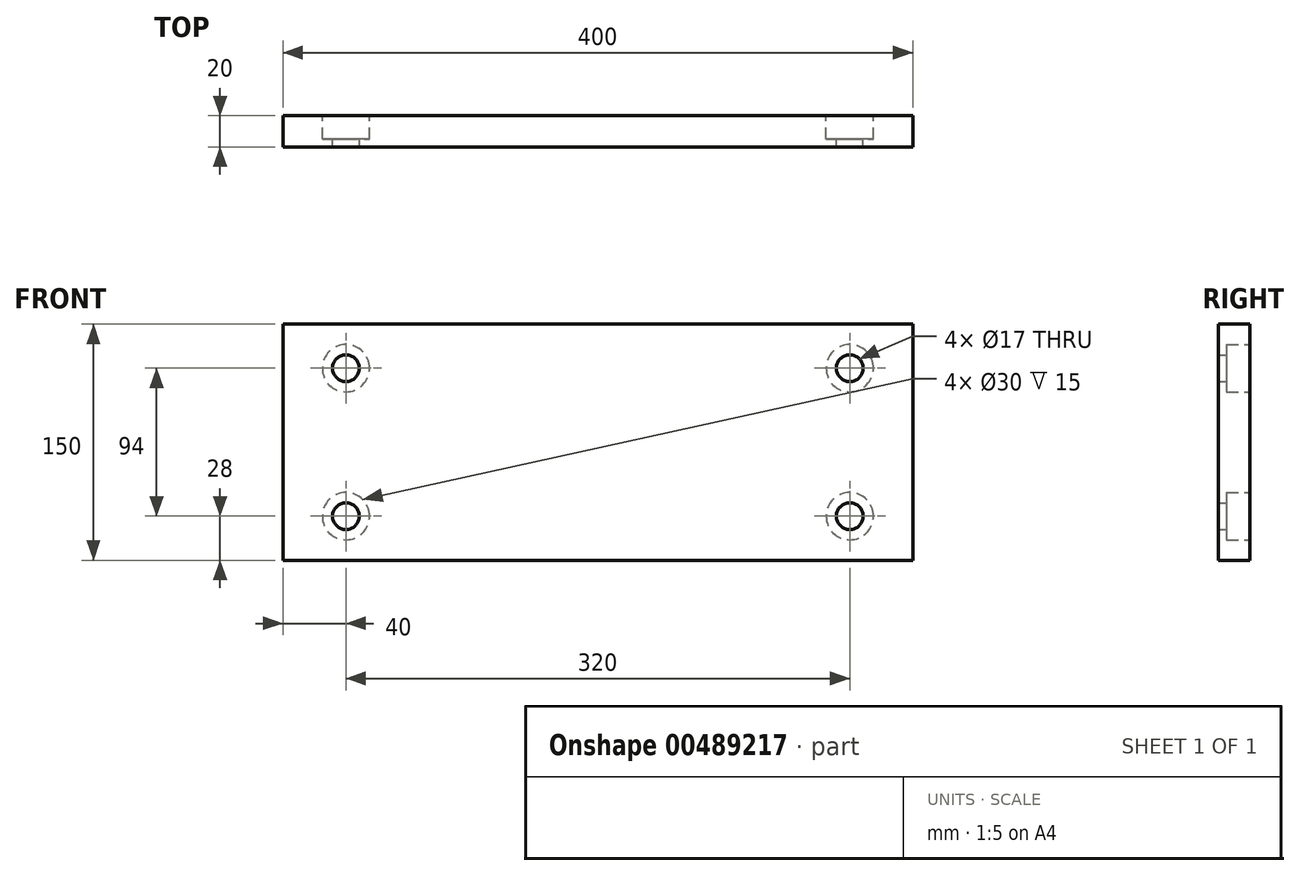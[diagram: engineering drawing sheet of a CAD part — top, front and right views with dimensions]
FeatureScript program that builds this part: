
annotation { "Feature Type Name" : "Feature", "Feature Type Description" : "" }
export const myFeature = defineFeature(function(context is Context, id is Id, definition is map)
    precondition{}
    {
        {
            var Q0;
            Q0=qCreatedBy(makeId("Front.planeOp"),FACE);
            var sketch = newSketch(context, id + "F0", { "sketchPlane" : qUnion([Q0])});
            skLineSegment(sketch, "E0.bottom", {"start": v(0, 0) * mm, "end": v(400, 0) * mm});
            skLineSegment(sketch, "E0.top", {"start": v(0, 150) * mm, "end": v(400, 150) * mm});
            skLineSegment(sketch, "E0.left", {"start": v(0, 0) * mm, "end": v(0, 150) * mm});
            skLineSegment(sketch, "E0.right", {"start": v(400, 0) * mm, "end": v(400, 150) * mm});
            skPoint(sketch, "E1.centerSnap0", {"position": v(400, 75) * mm});
            skPoint(sketch, "E1.centerSnap1", {"position": v(200, 0) * mm});
            skLineSegment(sketch, "E2", {"start": v(200, 75) * mm, "end": v(0, 75) * mm, "construction": true});
            skPoint(sketch, "E3", {"position": v(40, 122) * mm});
            skPoint(sketch, "E4.MirrorP", {"position": v(40, 28) * mm});
            skLineSegment(sketch, "E5", {"start": v(200, 75) * mm, "end": v(200, 182.53) * mm, "construction": true});
            skPoint(sketch, "E5.endSnap0", {"position": v(200, 150) * mm});
            skPoint(sketch, "E6.MirrorP", {"position": v(360, 28) * mm});
            skPoint(sketch, "E7.MirrorP", {"position": v(360, 122) * mm});
            skSolve(sketch);
        }
        {
            var Q0;
            Q0=makeQuery(id+"F0.imprint","IMPRINT",FACE,{"disambiguationData":[TD([[makeQuery(id+"F0.imprint","IMPRINT",EDGE,{"derivedFrom":sQuery(id+"F0.wireOp",EDGE,"E0.bottom")}),1.0]])]});
            extrude(context, id + "F1", {"entities" : qUnion([Q0]), "depth" : 20 * mm, "offsetDistance" : 25 * mm});
        }
        {
            var Q0;
            Q0=sQuery(id+"F0.wireOp",VERTEX,"E7.MirrorP");
            var Q1;
            Q1=sQuery(id+"F0.wireOp",VERTEX,"E6.MirrorP");
            var Q2;
            Q2=sQuery(id+"F0.wireOp",VERTEX,"E3");
            var Q3;
            Q3=sQuery(id+"F0.wireOp",VERTEX,"E4.MirrorP");
            var Q4;
            Q4=makeQuery(id+"F1.opExtrude","SWEPT_BODY",BODY,{"disambiguationData":[OSD([sQuery(id+"F0.wireOp",EDGE,"E0.bottom"),sQuery(id+"F0.wireOp",EDGE,"E0.top"),sQuery(id+"F0.wireOp",EDGE,"E0.left"),sQuery(id+"F0.wireOp",EDGE,"E0.right"),sQuery(id+"F0.wireOp",EDGE,"E1")])]});
            hole(context, id + "F2", {"style" : HoleStyle.C_BORE, "endStyle" : HoleEndStyle.BLIND, "oppositeDirection" : true, "standardTappedOrClearance" : lookupTablePath({ "standard" : "ISO", "size" : "17", "type" : "Drilled" }), "standardBlindInLast" : lookupTablePath({ "standard" : "ISO", "size" : "17", "type" : "Drilled" }), "holeDiameter" : 17 * mm, "cBoreDiameter" : 30 * mm, "cBoreDepth" : 15 * mm, "majorDiameter" : 16 * mm, "holeDepth" : 35 * mm, "isTappedThrough" : true, "tappedDepth" : 25 * mm, "tapClearance" : 5, "startFromSketch" : true, "locations" : qUnion([Q0, Q1, Q2, Q3]), "scope" : qUnion([Q4])});
        }
    });
